# Revit family: DCST_Счетчик водяной бытовой_ВСКМ iWAN
name_source: partatom
category: Арматура трубопроводов
units: mm (PartAtom-declared; Revit-internal decimal feet)

## family parameters
Всегда вертикально = Да
На основе рабочей плоскости = Нет
Общий = Нет
При загрузке вырезать с полостями = Нет
Размер круглого соединителя = Использовать диаметр
Тип детали = Вставляется

## types (3) — shared parameters
ADSK_Единица измерения = шт.
ADSK_Завод-изготовитель = Декаст
ADSK_Количество = 1
D = 20 мм
LT = ВСКМ iWAN
URL = https://www.decast.com
ИПД_Lo_B = ♦ : LoRaWAN, класс «B»
ИПД_Lo_C = ♦ : LoRaWAN, класс «C»
ИПД_NB = ♦ : NB-IoT
ИПД_RS = ♦ : RS-485
Изготовитель = Декаст

## per-type parameters (varying)
| type | ADSK_Диаметр условный | D1 | Dm | F | L1 | L2 | SW | Диаметр условного прохода | Монтажная длина | УГО_Высота | УГО_Длина | УГО_Длина линии |
| ВСКМ-15 iWAN 80 мм | 15 мм | 24 мм | 20 мм | 0 мм | 27 мм | 13 мм | 30 мм | 15 мм | 80 мм | 48 мм | 96 мм | 27 мм |
| ВСКМ-15 iWAN 110 мм | 15 мм | 24 мм | 20 мм | 0 мм | 27 мм | 13 мм | 30 мм | 15 мм | 110 мм | 63 мм | 126 мм | 27 мм |
| ВСКМ-20 iWAN 130 мм | 20 мм | 20 мм | 25 мм | 8 мм | 40 мм | 17 мм | 35 мм | 20 мм | 130 мм | 77 мм | 154 мм | 40 мм |
